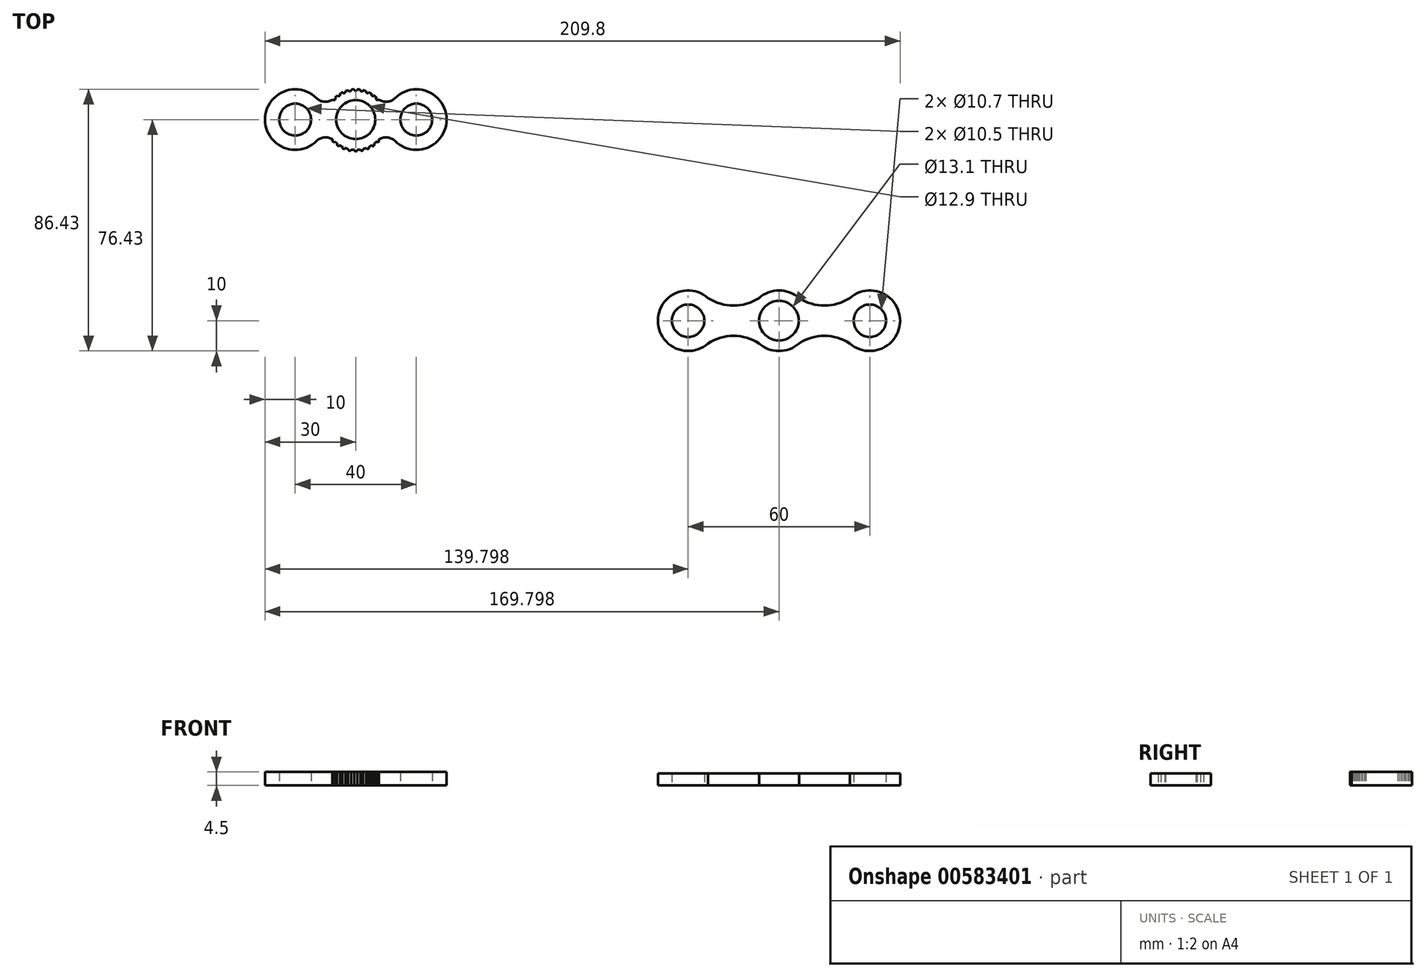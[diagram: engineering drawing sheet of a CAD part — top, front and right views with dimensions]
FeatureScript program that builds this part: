
annotation { "Feature Type Name" : "Feature", "Feature Type Description" : "" }
export const myFeature = defineFeature(function(context is Context, id is Id, definition is map)
    precondition{}
    {
        {
            var Q0;
            Q0=qCreatedBy(makeId("Top.planeOp"),FACE);
            var sketch = newSketch(context, id + "F0", { "sketchPlane" : qUnion([Q0])});
            skCircle(sketch, "E0", {"center": v(0, 0) * mm, "radius": 6.45 * mm});
            skLineSegment(sketch, "E1.left", {"start": v(30, 0) * mm, "end": v(30, 0) * mm});
            skLineSegment(sketch, "E1.right", {"start": v(-30, 0) * mm, "end": v(-30, 0) * mm});
            skPoint(sketch, "E2.endSnap0", {"position": v(-30, 0) * mm});
            skCircle(sketch, "E3", {"center": v(-20, 0) * mm, "radius": 5.25 * mm});
            skCircle(sketch, "E4", {"center": v(20, 0) * mm, "radius": 5.25 * mm});
            skPoint(sketch, "E5.visualSharp", {"position": v(30, 10) * mm});
            skPoint(sketch, "E6.visualSharp", {"position": v(30, -10) * mm});
            skArc(sketch, "E6.filletArc", {"start": v(20, -10) * mm, "mid": v(27.07, -7.07) * mm, "end": v(30, 0) * mm});
            skPoint(sketch, "E7.visualSharp", {"position": v(-30, 10) * mm});
            skArc(sketch, "E7.filletArc", {"start": v(-20, 10) * mm, "mid": v(-27.07, 7.07) * mm, "end": v(-30, 0) * mm});
            skPoint(sketch, "E8.visualSharp", {"position": v(-30, -10) * mm});
            skArc(sketch, "E8.filletArc", {"start": v(-30, 0) * mm, "mid": v(-27.07, -7.07) * mm, "end": v(-20, -10) * mm});
            skArc(sketch, "E9", {"start": v(-12.93, 7.07) * mm, "mid": v(-30, 0) * mm, "end": v(-12.93, -7.07) * mm});
            skArc(sketch, "E10", {"start": v(12.93, -7.07) * mm, "mid": v(16.17, -9.24) * mm, "end": v(20, -10) * mm});
            skArc(sketch, "E11", {"start": v(-12.93, 7.07) * mm, "mid": v(-10.33, 5.87) * mm, "end": v(-7.57, 6.64) * mm});
            skArc(sketch, "E12", {"start": v(-7.07, -7.07) * mm, "mid": v(-10, -5.86) * mm, "end": v(-12.93, -7.07) * mm});
            skArc(sketch, "E13", {"start": v(12.93, -7.07) * mm, "mid": v(10, -5.86) * mm, "end": v(7.07, -7.07) * mm});
            skArc(sketch, "E14.trimOffspring", {"start": v(-7.07, -7.07) * mm, "mid": v(0, -10) * mm, "end": v(7.07, -7.07) * mm});
            skArc(sketch, "E15", {"start": v(6.83, 7.3) * mm, "mid": v(6.45, 7.64) * mm, "end": v(6.06, 7.95) * mm});
            skArc(sketch, "E16.trimOffspring", {"start": v(30, 0) * mm, "mid": v(23.83, 9.24) * mm, "end": v(12.93, 7.07) * mm});
            skArc(sketch, "E17", {"start": v(-0.5, 9.99) * mm, "mid": v(0, 9.5) * mm, "end": v(0.5, 9.99) * mm});
            skArc(sketch, "E18", {"start": v(1.5, 9.89) * mm, "mid": v(1.9, 9.3) * mm, "end": v(2.48, 9.69) * mm});
            skArc(sketch, "E19", {"start": v(-2.48, 9.69) * mm, "mid": v(-1.9, 9.3) * mm, "end": v(-1.5, 9.89) * mm});
            skArc(sketch, "E20", {"start": v(3.44, 9.4) * mm, "mid": v(3.7, 8.75) * mm, "end": v(4.36, 9) * mm});
            skArc(sketch, "E21", {"start": v(5.24, 8.52) * mm, "mid": v(5.37, 7.84) * mm, "end": v(6.06, 7.95) * mm});
            skArc(sketch, "E22", {"start": v(6.83, 7.3) * mm, "mid": v(6.85, 6.59) * mm, "end": v(7.57, 6.64) * mm});
            skArc(sketch, "E23.MirrorC", {"start": v(-3.44, 9.4) * mm, "mid": v(-3.7, 8.75) * mm, "end": v(-4.36, 9) * mm});
            skArc(sketch, "E24.MirrorC", {"start": v(-5.24, 8.52) * mm, "mid": v(-5.37, 7.84) * mm, "end": v(-6.06, 7.95) * mm});
            skArc(sketch, "E25.MirrorC", {"start": v(-6.83, 7.3) * mm, "mid": v(-6.85, 6.59) * mm, "end": v(-7.57, 6.64) * mm});
            skCircle(sketch, "E26.MirrorC", {"center": v(7.19, -6.96) * mm, "radius": 0.5 * mm});
            skCircle(sketch, "E27.MirrorC", {"center": v(5.65, -8.25) * mm, "radius": 0.5 * mm});
            skCircle(sketch, "E28.MirrorC", {"center": v(3.9, -9.2) * mm, "radius": 0.5 * mm});
            skCircle(sketch, "E29.MirrorC", {"center": v(1.99, -9.8) * mm, "radius": 0.5 * mm});
            skCircle(sketch, "E30.MirrorC", {"center": v(0, -10) * mm, "radius": 0.5 * mm});
            skCircle(sketch, "E31.MirrorC", {"center": v(-1.99, -9.8) * mm, "radius": 0.5 * mm});
            skCircle(sketch, "E32.MirrorC", {"center": v(-3.9, -9.2) * mm, "radius": 0.5 * mm});
            skCircle(sketch, "E33.MirrorC", {"center": v(-5.65, -8.25) * mm, "radius": 0.5 * mm});
            skCircle(sketch, "E34.MirrorC", {"center": v(-7.19, -6.96) * mm, "radius": 0.5 * mm});
            skArc(sketch, "E35.trimOffspring", {"start": v(-6.06, 7.95) * mm, "mid": v(-6.45, 7.64) * mm, "end": v(-6.83, 7.3) * mm});
            skArc(sketch, "E36.trimOffspring", {"start": v(-4.36, 9) * mm, "mid": v(-4.8, 8.77) * mm, "end": v(-5.24, 8.52) * mm});
            skArc(sketch, "E37.trimOffspring", {"start": v(-2.48, 9.69) * mm, "mid": v(-2.96, 9.55) * mm, "end": v(-3.44, 9.4) * mm});
            skArc(sketch, "E38.trimOffspring", {"start": v(-0.5, 9.99) * mm, "mid": v(-1, 9.95) * mm, "end": v(-1.5, 9.89) * mm});
            skArc(sketch, "E39.trimOffspring", {"start": v(1.5, 9.89) * mm, "mid": v(1, 9.95) * mm, "end": v(0.5, 9.99) * mm});
            skArc(sketch, "E40.trimOffspring", {"start": v(3.44, 9.4) * mm, "mid": v(2.96, 9.55) * mm, "end": v(2.48, 9.69) * mm});
            skArc(sketch, "E41.trimOffspring", {"start": v(5.24, 8.52) * mm, "mid": v(4.8, 8.77) * mm, "end": v(4.36, 9) * mm});
            skArc(sketch, "E42.trimOffspring", {"start": v(7.57, 6.64) * mm, "mid": v(10.33, 5.87) * mm, "end": v(12.93, 7.07) * mm});
            skSolve(sketch);
        }
        {
            var Q0;
            Q0 = qSketchRegion(id + "F0", true);
            extrude(context, id + "F1", {"entities" : qUnion([Q0]), "depth" : 4.5 * mm, "offsetDistance" : 25 * mm});
        }
        {
            var Q0;
            Q0=qCreatedBy(makeId("Right.planeOp"),FACE);
            var sketch = newSketch(context, id + "F2", { "sketchPlane" : qUnion([Q0])});
            skLineSegment(sketch, "E43", {"start": v(25.36, 0) * mm, "end": v(25.36, 2.3) * mm});
            skLineSegment(sketch, "E44", {"start": v(25.36, 2.3) * mm, "end": v(26.36, 2.3) * mm});
            skLineSegment(sketch, "E45", {"start": v(26.36, 2.3) * mm, "end": v(26.36, 3.1) * mm});
            skLineSegment(sketch, "E46", {"start": v(22.26, 4.8) * mm, "end": v(31.76, 4.8) * mm});
            skLineSegment(sketch, "E47", {"start": v(32.26, 4.3) * mm, "end": v(32.26, 3.6) * mm});
            skLineSegment(sketch, "E48", {"start": v(31.76, 3.1) * mm, "end": v(26.36, 3.1) * mm});
            skPoint(sketch, "E49.visualSharp", {"position": v(32.26, 4.8) * mm});
            skArc(sketch, "E49.filletArc", {"start": v(32.26, 4.3) * mm, "mid": v(32.11, 4.65) * mm, "end": v(31.76, 4.8) * mm});
            skPoint(sketch, "E50.visualSharp", {"position": v(32.26, 3.1) * mm});
            skArc(sketch, "E50.filletArc", {"start": v(31.76, 3.1) * mm, "mid": v(32.11, 3.25) * mm, "end": v(32.26, 3.6) * mm});
            skLineSegment(sketch, "E51", {"start": v(22.26, 4.8) * mm, "end": v(22.26, 0) * mm});
            skLineSegment(sketch, "E52", {"start": v(22.26, 0) * mm, "end": v(25.36, 0) * mm});
            skSolve(sketch);
        }
        {
            var Q0;
            Q0=qCreatedBy(makeId("Top.planeOp"),FACE);
            var sketch = newSketch(context, id + "F3", { "sketchPlane" : qUnion([Q0])});
            skCircle(sketch, "E53", {"center": v(169.8, -66.43) * mm, "radius": 5.35 * mm});
            skArc(sketch, "E54", {"start": v(163.18, -73.93) * mm, "mid": v(179.8, -66.43) * mm, "end": v(163.18, -58.93) * mm});
            skArc(sketch, "E55", {"start": v(116.41, -58.93) * mm, "mid": v(99.8, -66.43) * mm, "end": v(116.41, -73.93) * mm});
            skCircle(sketch, "E56", {"center": v(109.8, -66.43) * mm, "radius": 5.35 * mm});
            skCircle(sketch, "E57", {"center": v(139.8, -66.43) * mm, "radius": 6.55 * mm});
            skArc(sketch, "E58", {"start": v(133.18, -73.93) * mm, "mid": v(139.8, -76.43) * mm, "end": v(146.41, -73.93) * mm});
            skArc(sketch, "E59", {"start": v(116.41, -58.93) * mm, "mid": v(124.8, -61.43) * mm, "end": v(133.18, -58.93) * mm});
            skArc(sketch, "E60", {"start": v(133.18, -73.93) * mm, "mid": v(124.8, -71.43) * mm, "end": v(116.41, -73.93) * mm});
            skArc(sketch, "E61", {"start": v(146.41, -58.93) * mm, "mid": v(154.8, -61.43) * mm, "end": v(163.18, -58.93) * mm});
            skArc(sketch, "E62", {"start": v(163.18, -73.93) * mm, "mid": v(154.8, -71.43) * mm, "end": v(146.41, -73.93) * mm});
            skArc(sketch, "E63.trimOffspring", {"start": v(146.41, -58.93) * mm, "mid": v(139.8, -56.43) * mm, "end": v(133.18, -58.93) * mm});
            skPoint(sketch, "E64", {"position": v(99.8, -66.43) * mm});
            skPoint(sketch, "E65", {"position": v(179.8, -66.43) * mm});
            skSolve(sketch);
        }
        {
            var Q0;
            Q0 = qSketchRegion(id + "F3", true);
            extrude(context, id + "F4", {"entities" : qUnion([Q0]), "depth" : 4 * mm, "offsetDistance" : 25 * mm});
        }
    });
